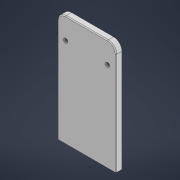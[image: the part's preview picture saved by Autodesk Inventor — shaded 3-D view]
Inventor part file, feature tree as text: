
AUTODESK INVENTOR PART (.ipt)
format: ipt  version: 2021 (Build 250183000, 183)  size: 120,320 bytes
history: native  units: mm
features: sketch x2, extrude x1, fillet x1, hole x1, chamfer x1
ambient origin geometry x8: Origin, YZ Plane, XZ Plane, XY Plane, X Axis, Y Axis, Z Axis, Center Point
bodies: Solid1 (feature_tree)
feature tree (6):
  extrude  "Extrusion1"  Depth=35.0mm
  fillet  "Fillet1"  Radius=132.0mm
  hole  "Hole1"  [1 undecoded]
  chamfer  "Chamfer1"  Distance=70.0mm
  sketch  "Sketch1"  dims[d0=70.0mm d1=35.0mm d2=132.0mm]
  sketch  "Sketch2"  dims[d3=8.0mm d4=0.0mm d5=10.0mm d6=70.0mm d9=50.0mm d10=0.0mm d11=10.0mm d13=106.6mm d14=5.0mm d15=6.0mm d16=4.0mm d17=2.0mm d18=90.0deg d19=8.0mm d20=0.0mm d21=1.0mm d22=2.0mm d23=45.0deg]
note: 1 required parameter value undecoded (feature->parameter linkage not recoverable at this tier; creation-order binding heuristic only, values carry confidence <= 0.55)
